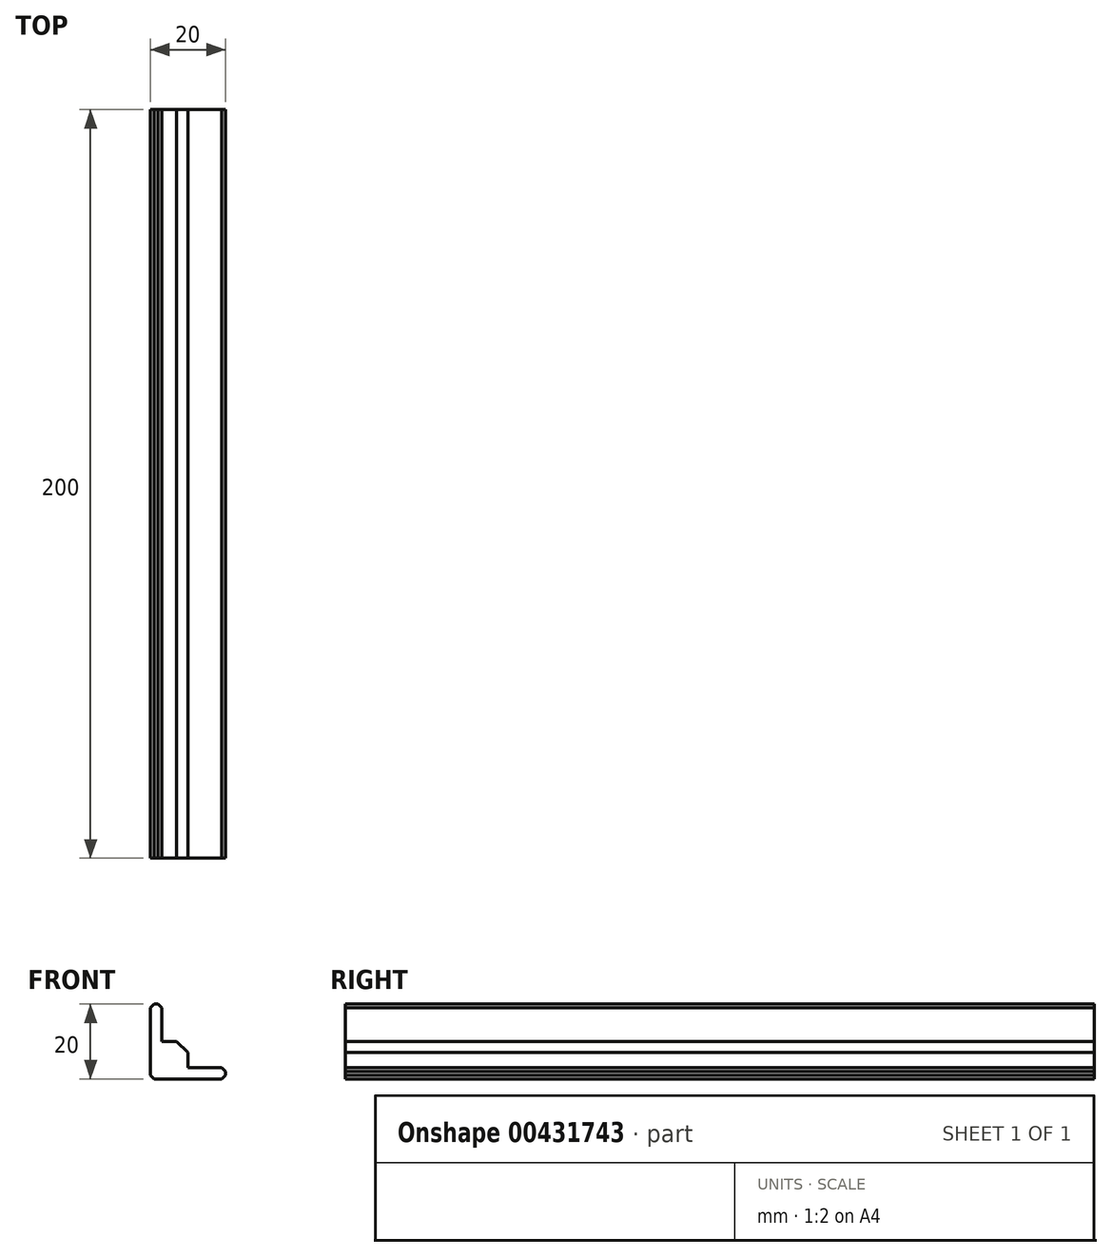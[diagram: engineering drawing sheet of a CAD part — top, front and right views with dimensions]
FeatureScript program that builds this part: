
annotation { "Feature Type Name" : "Feature", "Feature Type Description" : "" }
export const myFeature = defineFeature(function(context is Context, id is Id, definition is map)
    precondition{}
    {
        {
            var Q0;
            Q0=qCreatedBy(makeId("Front.planeOp"),FACE);
            var sketch = newSketch(context, id + "F0", { "sketchPlane" : qUnion([Q0])});
            skLineSegment(sketch, "E0", {"start": v(0, 0) * mm, "end": v(0, 20) * mm});
            skLineSegment(sketch, "E1", {"start": v(0, 0) * mm, "end": v(20, 0) * mm});
            skLineSegment(sketch, "E2", {"start": v(0, 20) * mm, "end": v(3, 20) * mm});
            skLineSegment(sketch, "E3", {"start": v(20, 0) * mm, "end": v(20, 3) * mm});
            skLineSegment(sketch, "E4", {"start": v(3, 20) * mm, "end": v(3, 10) * mm});
            skLineSegment(sketch, "E5", {"start": v(20, 3) * mm, "end": v(10, 3) * mm});
            skLineSegment(sketch, "E6", {"start": v(3, 10) * mm, "end": v(10, 10) * mm});
            skLineSegment(sketch, "E7", {"start": v(10, 3) * mm, "end": v(10, 10) * mm});
            skSolve(sketch);
        }
        {
            var Q0;
            Q0=makeQuery(id+"F0.imprint","IMPRINT",FACE,{"disambiguationData":[TD([[makeQuery(id+"F0.imprint","IMPRINT",EDGE,{"derivedFrom":sQuery(id+"F0.wireOp",EDGE,"E0")}),-1.0]])]});
            extrude(context, id + "F1", {"entities" : qUnion([Q0]), "depth" : 200 * mm});
        }
        {
            var Q0;
            Q0=makeQuery(id+"F1.opExtrude","SWEPT_EDGE",EDGE,{"disambiguationData":[OSD([sQuery(id+"F0.wireOp",EDGE,"E0"),sQuery(id+"F0.wireOp",EDGE,"E2")])]});
            var Q1;
            Q1=makeQuery(id+"F1.opExtrude","SWEPT_EDGE",EDGE,{"disambiguationData":[OSD([sQuery(id+"F0.wireOp",EDGE,"E2"),sQuery(id+"F0.wireOp",EDGE,"E4")])]});
            var Q2;
            Q2=makeQuery(id+"F1.opExtrude","SWEPT_EDGE",EDGE,{"disambiguationData":[OSD([sQuery(id+"F0.wireOp",EDGE,"E3"),sQuery(id+"F0.wireOp",EDGE,"E5")])]});
            var Q3;
            Q3=makeQuery(id+"F1.opExtrude","SWEPT_EDGE",EDGE,{"disambiguationData":[OSD([sQuery(id+"F0.wireOp",EDGE,"E1"),sQuery(id+"F0.wireOp",EDGE,"E3")])]});
            var Q4;
            Q4=makeQuery(id+"F1.opExtrude","SWEPT_EDGE",EDGE,{"disambiguationData":[OSD([sQuery(id+"F0.wireOp",EDGE,"E0"),sQuery(id+"F0.wireOp",EDGE,"E1")])]});
            chamfer(context, id + "F2", {"entities" : qUnion([Q0, Q1, Q2, Q3, Q4]), "width" : 1 * mm, "tangentPropagation" : true});
        }
        {
            var Q0;
            Q0=makeQuery(id+"F1.opExtrude","SWEPT_EDGE",EDGE,{"disambiguationData":[OSD([sQuery(id+"F0.wireOp",EDGE,"E6"),sQuery(id+"F0.wireOp",EDGE,"E7")])]});
            chamfer(context, id + "F3", {"entities" : qUnion([Q0]), "width" : 3 * mm, "tangentPropagation" : true});
        }
    });
